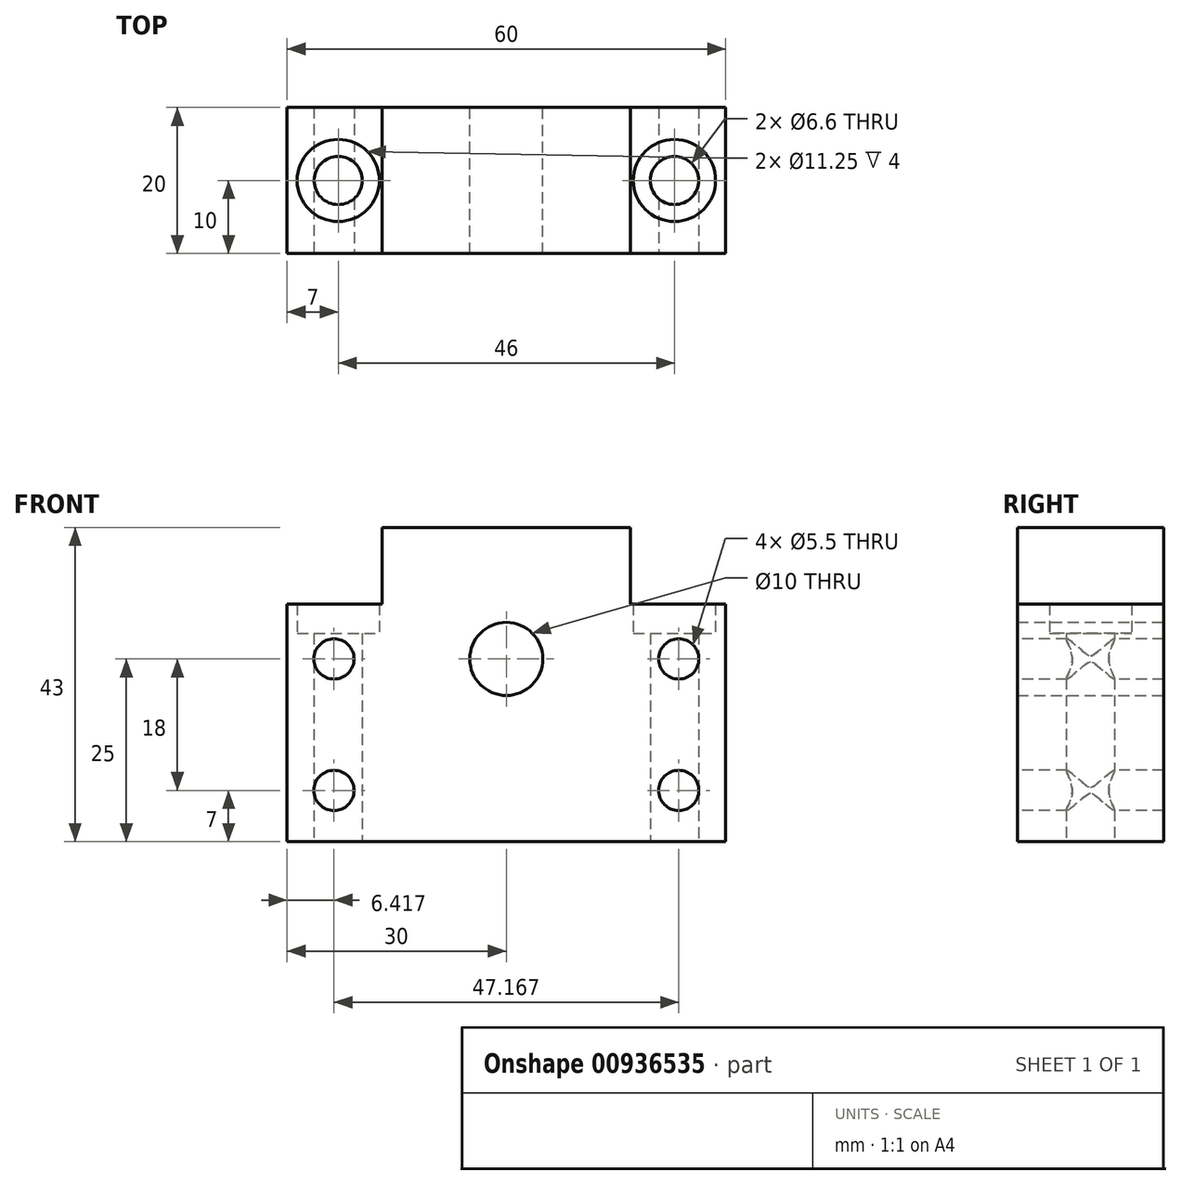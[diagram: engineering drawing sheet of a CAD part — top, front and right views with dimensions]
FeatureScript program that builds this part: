
annotation { "Feature Type Name" : "Feature", "Feature Type Description" : "" }
export const myFeature = defineFeature(function(context is Context, id is Id, definition is map)
    precondition{}
    {
        {
            var Q0;
            Q0=qCreatedBy(makeId("Front.planeOp"),FACE);
            var sketch = newSketch(context, id + "F0", { "sketchPlane" : qUnion([Q0])});
            skLineSegment(sketch, "E0.bottom", {"start": v(30, 16.25) * mm, "end": v(17, 16.25) * mm});
            skLineSegment(sketch, "E0.top", {"start": v(30, -16.25) * mm, "end": v(-30, -16.25) * mm});
            skLineSegment(sketch, "E0.left", {"start": v(30, 16.25) * mm, "end": v(30, -16.25) * mm});
            skLineSegment(sketch, "E0.right", {"start": v(-30, 16.25) * mm, "end": v(-30, -16.25) * mm});
            skPoint(sketch, "E0.middle", {"position": v(0, 0) * mm});
            skLineSegment(sketch, "E1.bottom", {"start": v(17, 26.75) * mm, "end": v(-17, 26.75) * mm});
            skLineSegment(sketch, "E1.left", {"start": v(17, 26.75) * mm, "end": v(17, 16.25) * mm});
            skLineSegment(sketch, "E1.right", {"start": v(-17, 26.75) * mm, "end": v(-17, 16.25) * mm});
            skPoint(sketch, "E1.middle", {"position": v(0, 8.75) * mm});
            skCircle(sketch, "E2", {"center": v(0, 8.75) * mm, "radius": 5 * mm});
            skLineSegment(sketch, "E3.trimOffspring", {"start": v(-17, 16.25) * mm, "end": v(-30, 16.25) * mm});
            skPoint(sketch, "E4", {"position": v(23.58, -9.25) * mm});
            skPoint(sketch, "E5", {"position": v(23.58, 8.75) * mm});
            skPoint(sketch, "E6.MirrorP", {"position": v(-23.58, 8.75) * mm});
            skPoint(sketch, "E7.MirrorP", {"position": v(-23.58, -9.25) * mm});
            skSolve(sketch);
        }
        {
            var Q0;
            Q0=makeQuery(id+"F0.imprint","IMPRINT",FACE,{"disambiguationData":[TD([[makeQuery(id+"F0.imprint","IMPRINT",EDGE,{"derivedFrom":sQuery(id+"F0.wireOp",EDGE,"E0.bottom")}),1.0]])]});
            extrude(context, id + "F1", {"entities" : qUnion([Q0]), "depth" : 20 * mm, "offsetDistance" : 25 * mm});
        }
        {
            var Q0;
            Q0=makeQuery(id+"F1.opExtrude","SWEPT_FACE",FACE,{"disambiguationData":[OSD([sQuery(id+"F0.wireOp",EDGE,"E0.bottom")])]});
            var sketch = newSketch(context, id + "F2", { "sketchPlane" : qUnion([Q0])});
            skPoint(sketch, "E8", {"position": v(23, -10) * mm});
            skPoint(sketch, "E9.MirrorP", {"position": v(-23, -10) * mm});
            skSolve(sketch);
        }
        {
            var Q0;
            Q0=sQuery(id+"F2.wireOp",VERTEX,"E9.MirrorP");
            var Q1;
            Q1=sQuery(id+"F2.wireOp",VERTEX,"E8");
            var Q2;
            Q2=makeQuery(id+"F1.opExtrude","SWEPT_BODY",BODY,{"disambiguationData":[OSD([sQuery(id+"F0.wireOp",EDGE,"E0.bottom"),sQuery(id+"F0.wireOp",EDGE,"E0.top"),sQuery(id+"F0.wireOp",EDGE,"E0.left"),sQuery(id+"F0.wireOp",EDGE,"E0.right"),sQuery(id+"F0.wireOp",EDGE,"E1.bottom"),sQuery(id+"F0.wireOp",EDGE,"E1.left"),sQuery(id+"F0.wireOp",EDGE,"E1.right"),sQuery(id+"F0.wireOp",EDGE,"E2"),sQuery(id+"F0.wireOp",EDGE,"E3.trimOffspring")])]});
            hole(context, id + "F3", {"style" : HoleStyle.C_BORE, "endStyle" : HoleEndStyle.THROUGH, "holeDiameter" : 6.6 * mm, "cBoreDiameter" : 11.25 * mm, "cBoreDepth" : 4 * mm, "majorDiameter" : 5 * mm, "tappedDepth" : 12 * mm, "tapClearance" : 3, "locations" : qUnion([Q0, Q1]), "scope" : qUnion([Q2]), "startStyle" : HoleStartStyle.PART});
        }
        {
            var Q0;
            Q0=sQuery(id+"F0.wireOp",VERTEX,"E5");
            var Q1;
            Q1=sQuery(id+"F0.wireOp",VERTEX,"E4");
            var Q2;
            Q2=sQuery(id+"F0.wireOp",VERTEX,"E7.MirrorP");
            var Q3;
            Q3=sQuery(id+"F0.wireOp",VERTEX,"E6.MirrorP");
            var Q4;
            Q4=makeQuery(id+"F1.opExtrude","SWEPT_BODY",BODY,{"disambiguationData":[OSD([sQuery(id+"F0.wireOp",EDGE,"E0.bottom"),sQuery(id+"F0.wireOp",EDGE,"E0.top"),sQuery(id+"F0.wireOp",EDGE,"E0.left"),sQuery(id+"F0.wireOp",EDGE,"E0.right"),sQuery(id+"F0.wireOp",EDGE,"E1.bottom"),sQuery(id+"F0.wireOp",EDGE,"E1.left"),sQuery(id+"F0.wireOp",EDGE,"E1.right"),sQuery(id+"F0.wireOp",EDGE,"E2"),sQuery(id+"F0.wireOp",EDGE,"E3.trimOffspring")])]});
            hole(context, id + "F4", {"style" : HoleStyle.SIMPLE, "endStyle" : HoleEndStyle.THROUGH, "oppositeDirection" : true, "standardTappedOrClearance" : lookupTablePath({ "fit" : "Normal", "standard" : "ISO", "size" : "M5", "type" : "Clearance" }), "standardBlindInLast" : lookupTablePath({ "fit" : "Standard", "standard" : "ISO", "size" : "M5", "type" : "Clearance" }), "holeDiameter" : 5.5 * mm, "majorDiameter" : 5 * mm, "tappedDepth" : 12 * mm, "tapClearance" : 3, "locations" : qUnion([Q0, Q1, Q2, Q3]), "scope" : qUnion([Q4]), "startStyle" : HoleStartStyle.PART});
        }
    });
